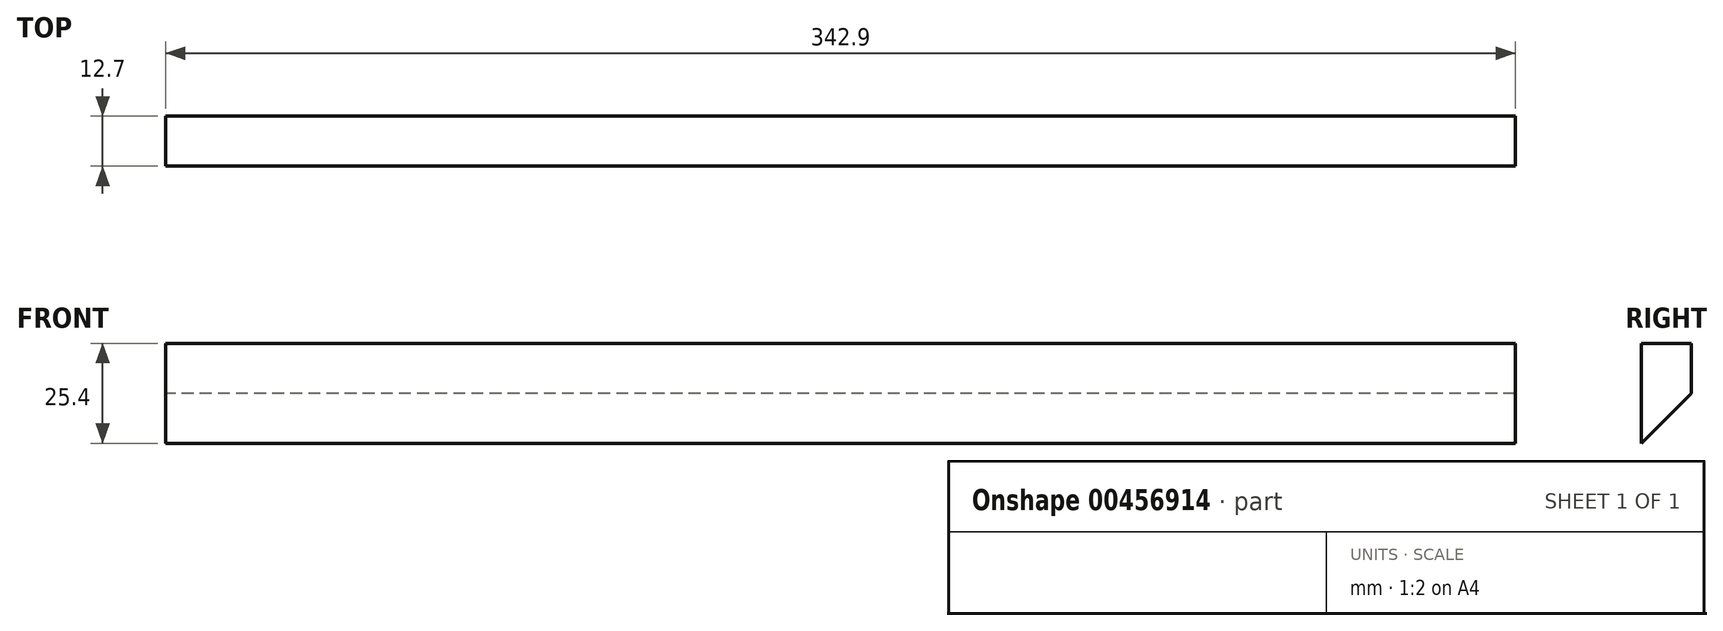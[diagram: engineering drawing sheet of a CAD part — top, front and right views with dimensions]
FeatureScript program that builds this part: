
annotation { "Feature Type Name" : "Feature", "Feature Type Description" : "" }
export const myFeature = defineFeature(function(context is Context, id is Id, definition is map)
    precondition{}
    {
        {
            var Q0;
            Q0=qCreatedBy(makeId("Right.planeOp"),FACE);
            var sketch = newSketch(context, id + "F0", { "sketchPlane" : qUnion([Q0])});
            skLineSegment(sketch, "E0.bottom", {"start": v(-7.86, 1.06) * mm, "end": v(4.84, 1.06) * mm});
            skLineSegment(sketch, "E0.left", {"start": v(-7.86, 1.06) * mm, "end": v(-7.86, -24.34) * mm});
            skLineSegment(sketch, "E0.right", {"start": v(4.84, 1.06) * mm, "end": v(4.84, -11.64) * mm});
            skLineSegment(sketch, "E1", {"start": v(-7.86, -24.34) * mm, "end": v(4.84, -11.64) * mm});
            skSolve(sketch);
        }
        {
            var Q0;
            Q0=makeQuery(id+"F0.imprint","IMPRINT",FACE,{"disambiguationData":[TD([[makeQuery(id+"F0.imprint","IMPRINT",EDGE,{"derivedFrom":sQuery(id+"F0.wireOp",EDGE,"E0.bottom")}),-1.0]])]});
            extrude(context, id + "F1", {"entities" : qUnion([Q0]), "depth" : 342.9 * mm});
        }
    });
